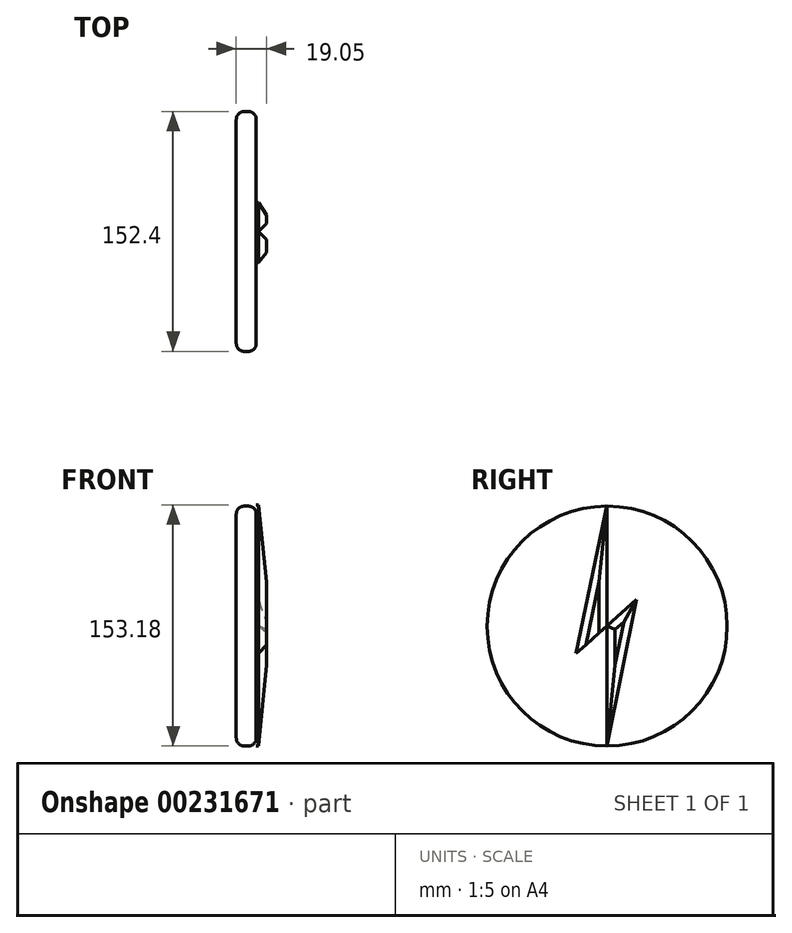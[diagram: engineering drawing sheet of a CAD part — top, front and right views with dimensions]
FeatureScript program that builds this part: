
annotation { "Feature Type Name" : "Feature", "Feature Type Description" : "" }
export const myFeature = defineFeature(function(context is Context, id is Id, definition is map)
    precondition{}
    {
        {
            var Q0;
            Q0=qCreatedBy(makeId("Right.planeOp"),FACE);
            var sketch = newSketch(context, id + "F0", { "sketchPlane" : qUnion([Q0])});
            skLineSegment(sketch, "E0", {"start": v(0, 76.98) * mm, "end": v(0, 0) * mm});
            skLineSegment(sketch, "E1", {"start": v(0, 76.98) * mm, "end": v(-19.87, -17.38) * mm});
            skLineSegment(sketch, "E2", {"start": v(-19.87, -17.38) * mm, "end": v(0, 0) * mm});
            skLineSegment(sketch, "E3", {"start": v(0, 0) * mm, "end": v(18.51, 16.93) * mm});
            skLineSegment(sketch, "E4", {"start": v(18.51, 16.93) * mm, "end": v(0, -76.08) * mm});
            skLineSegment(sketch, "E5", {"start": v(0, 0) * mm, "end": v(0, -76.08) * mm});
            skSolve(sketch);
        }
        {
            var Q0;
            Q0=makeQuery(id+"F0.imprint","IMPRINT",FACE,{"disambiguationData":[TD([[makeQuery(id+"F0.imprint","IMPRINT",EDGE,{"derivedFrom":sQuery(id+"F0.wireOp",EDGE,"E3")}),-1.0]])]});
            var Q1;
            Q1=makeQuery(id+"F0.imprint","IMPRINT",FACE,{"disambiguationData":[TD([[makeQuery(id+"F0.imprint","IMPRINT",EDGE,{"derivedFrom":sQuery(id+"F0.wireOp",EDGE,"E0")}),-1.0]])]});
            extrude(context, id + "F1", {"entities" : qUnion([Q0, Q1]), "depth" : 6.35 * mm});
        }
        {
            var Q0;
            Q0=qCreatedBy(makeId("Right.planeOp"),FACE);
            var sketch = newSketch(context, id + "F2", { "sketchPlane" : qUnion([Q0])});
            skCircle(sketch, "E6", {"center": v(0, 0) * mm, "radius": 76.2 * mm});
            skSolve(sketch);
        }
        {
            var Q0;
            Q0 = qSketchRegion(id + "F2", true);
            extrude(context, id + "F3", {"entities" : qUnion([Q0]), "oppositeDirection" : true, "depth" : 12.7 * mm});
        }
        {
            var Q0;
            Q0=makeQuery(id+"F3.opExtrude","CAP_EDGE",EDGE,{"disambiguationData":[OSD([sQuery(id+"F2.wireOp",EDGE,"E6")])],"isStart":true});
            var Q1;
            Q1=makeQuery(id+"F3.opExtrude","CAP_EDGE",EDGE,{"disambiguationData":[OSD([sQuery(id+"F2.wireOp",EDGE,"E6")])],"isStart":false});
            fillet(context, id + "F4", {"entities" : qUnion([Q0, Q1]), "radius" : 5.08 * mm, "tangentPropagation" : true, "allowEdgeOverflow" : false});
        }
        {
            var Q0;
            Q0=makeQuery(id+"F1.opExtrude","CAP_EDGE",EDGE,{"disambiguationData":[OSD([sQuery(id+"F0.wireOp",EDGE,"E1")])],"isStart":false});
            var Q1;
            Q1=makeQuery(id+"F1.opExtrude","CAP_EDGE",EDGE,{"disambiguationData":[OSD([sQuery(id+"F0.wireOp",EDGE,"E0")])],"isStart":false});
            var Q2;
            Q2=makeQuery(id+"F1.opExtrude","CAP_EDGE",EDGE,{"disambiguationData":[OSD([sQuery(id+"F0.wireOp",EDGE,"E5")])],"isStart":false});
            var Q3;
            Q3=makeQuery(id+"F1.opExtrude","CAP_EDGE",EDGE,{"disambiguationData":[OSD([sQuery(id+"F0.wireOp",EDGE,"E4")])],"isStart":false});
            var Q4;
            Q4=makeQuery(id+"F1.opExtrude","CAP_EDGE",EDGE,{"disambiguationData":[OSD([sQuery(id+"F0.wireOp",EDGE,"E3")])],"isStart":false});
            chamfer(context, id + "F5", {"entities" : qUnion([Q0, Q1, Q2, Q3, Q4]), "width" : 5.08 * mm, "tangentPropagation" : true});
        }
    });
